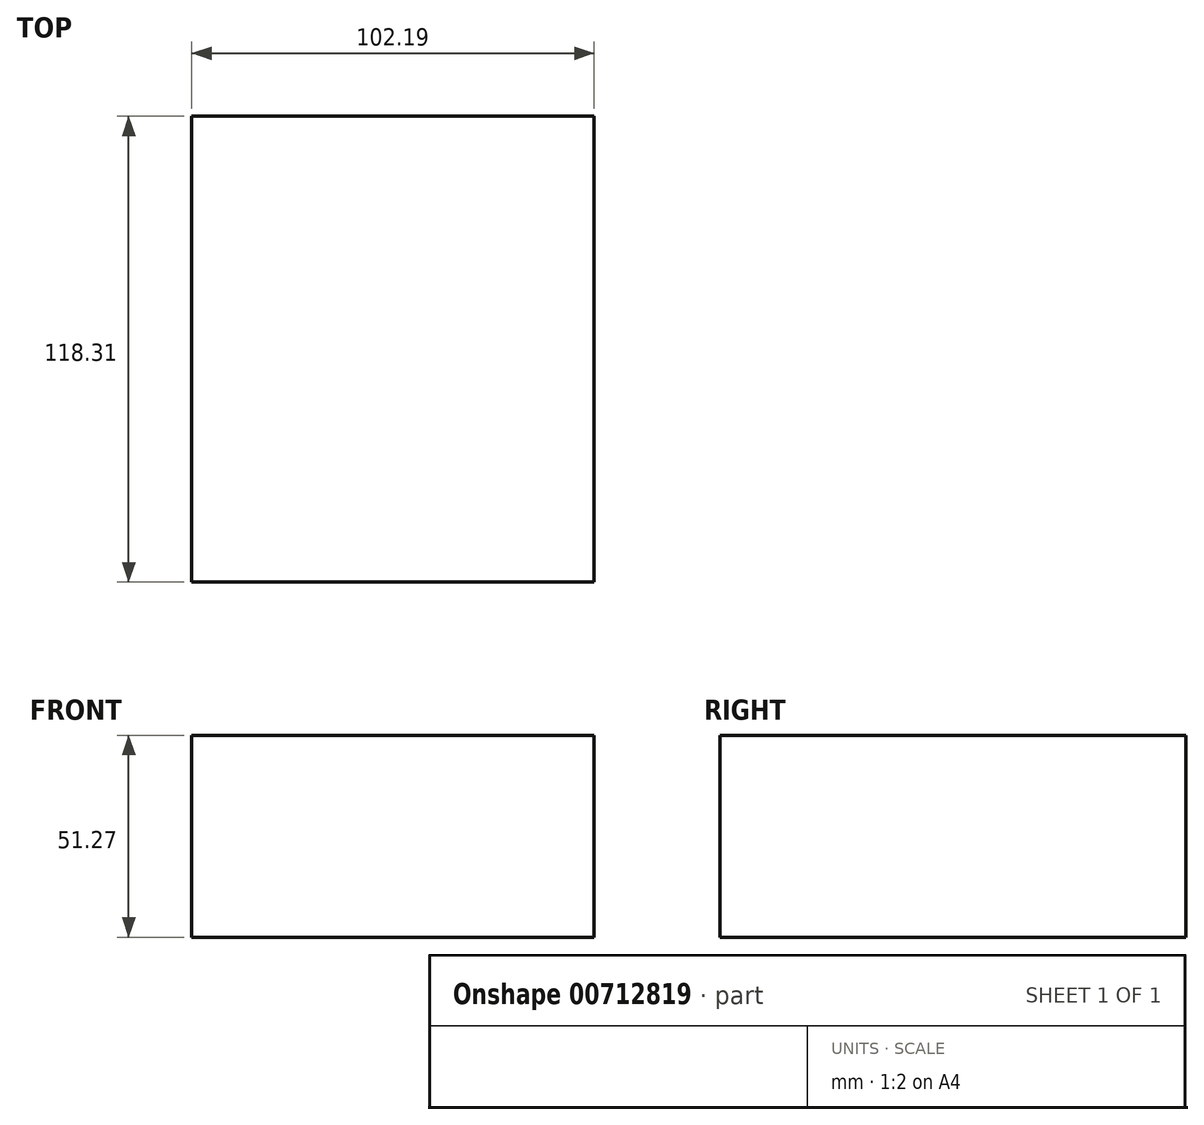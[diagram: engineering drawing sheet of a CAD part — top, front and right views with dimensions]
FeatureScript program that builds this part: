
annotation { "Feature Type Name" : "Feature", "Feature Type Description" : "" }
export const myFeature = defineFeature(function(context is Context, id is Id, definition is map)
    precondition{}
    {
        {
            var Q0;
            Q0=qCreatedBy(makeId("Top.planeOp"),FACE);
            var sketch = newSketch(context, id + "F0", { "sketchPlane" : qUnion([Q0])});
            skLineSegment(sketch, "E0.bottom", {"start": v(-31.88, 42.24) * mm, "end": v(-27.66, 42.24) * mm});
            skLineSegment(sketch, "E0.top", {"start": v(-31.88, 34.6) * mm, "end": v(-27.66, 34.6) * mm});
            skLineSegment(sketch, "E0.left", {"start": v(-31.88, 42.24) * mm, "end": v(-31.88, 34.6) * mm});
            skLineSegment(sketch, "E0.right", {"start": v(-27.66, 42.24) * mm, "end": v(-27.66, 34.6) * mm});
            skLineSegment(sketch, "E1.bottom", {"start": v(40.7, 30.76) * mm, "end": v(142.89, 30.76) * mm});
            skLineSegment(sketch, "E1.top", {"start": v(40.7, -87.55) * mm, "end": v(142.89, -87.55) * mm});
            skLineSegment(sketch, "E1.left", {"start": v(40.7, 30.76) * mm, "end": v(40.7, -87.55) * mm});
            skLineSegment(sketch, "E1.right", {"start": v(142.89, 30.76) * mm, "end": v(142.89, -87.55) * mm});
            skLineSegment(sketch, "E2.bottom", {"start": v(142.89, -28.4) * mm, "end": v(40.7, -28.4) * mm});
            skLineSegment(sketch, "E2.top", {"start": v(142.89, -51.62) * mm, "end": v(40.7, -51.62) * mm});
            skLineSegment(sketch, "E2.left", {"start": v(142.89, -51.62) * mm, "end": v(142.89, -28.4) * mm});
            skLineSegment(sketch, "E2.right", {"start": v(40.7, -51.62) * mm, "end": v(40.7, -28.4) * mm});
            skSolve(sketch);
        }
        {
            var Q0;
            Q0=sQuery(id+"F0.wireOp",EDGE,"E1.right");
            var Q1;
            Q1=sQuery(id+"F0.wireOp",EDGE,"E1.left");
            var Q2;
            Q2=sQuery(id+"F0.wireOp",EDGE,"E1.bottom");
            var Q3;
            Q3=sQuery(id+"F0.wireOp",EDGE,"E1.top");
            extrude(context, id + "F1", {"bodyType" : ToolBodyType.SURFACE, "surfaceEntities" : qUnion([Q0, Q1, Q2, Q3]), "depth" : 51.27 * mm, "offsetDistance" : 25.4 * mm});
        }
    });
